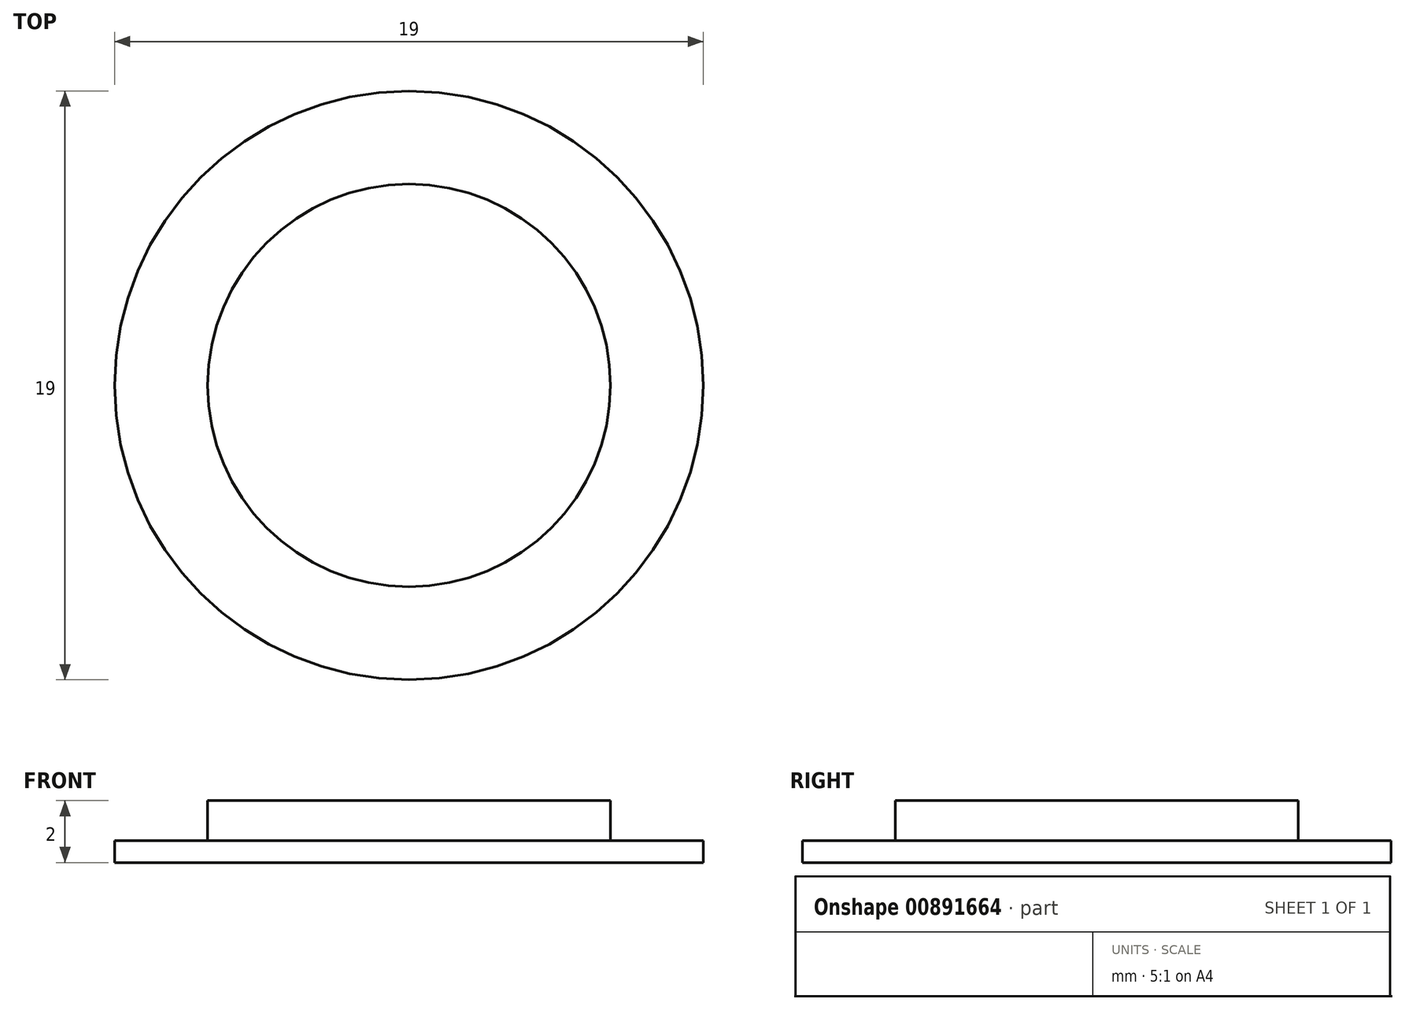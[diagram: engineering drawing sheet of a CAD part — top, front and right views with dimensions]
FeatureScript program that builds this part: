
annotation { "Feature Type Name" : "Feature", "Feature Type Description" : "" }
export const myFeature = defineFeature(function(context is Context, id is Id, definition is map)
    precondition{}
    {
        {
            var Q0;
            Q0=qCreatedBy(makeId("Right.planeOp"),FACE);
            var sketch = newSketch(context, id + "F0", { "sketchPlane" : qUnion([Q0])});
            skLineSegment(sketch, "E0", {"start": v(0, 0) * mm, "end": v(0, 2) * mm});
            skLineSegment(sketch, "E1", {"start": v(0, 2) * mm, "end": v(6.5, 2) * mm});
            skLineSegment(sketch, "E2", {"start": v(6.5, 2) * mm, "end": v(6.5, 0.7) * mm});
            skLineSegment(sketch, "E3", {"start": v(6.5, 0.7) * mm, "end": v(9.5, 0.7) * mm});
            skLineSegment(sketch, "E4", {"start": v(9.5, 0.7) * mm, "end": v(9.5, 0) * mm});
            skLineSegment(sketch, "E5", {"start": v(9.5, 0) * mm, "end": v(0, 0) * mm});
            skLineSegment(sketch, "E6", {"start": v(0, -24.46) * mm, "end": v(0, 8.55) * mm});
            skSolve(sketch);
        }
        {
            var Q0;
            {var subQ0=sQuery(id+"F0.wireOp",EDGE,"E1");Q0=makeQuery(id+"F0.imprint","IMPRINT",FACE,{"disambiguationData":[TD([[makeQuery(id+"F0.imprint","IMPRINT",EDGE,{"derivedFrom":subQ0}),-1.0]])]});}
            var Q1;
            Q1=sQuery(id+"F0.wireOp",EDGE,"E6");
            revolve(context, id + "F1", {"surfaceOperationType" : NewSurfaceOperationType.NEW, "entities" : qUnion([Q0]), "axis" : qUnion([Q1]), "revolveType" : RevolveType.FULL});
        }
    });
